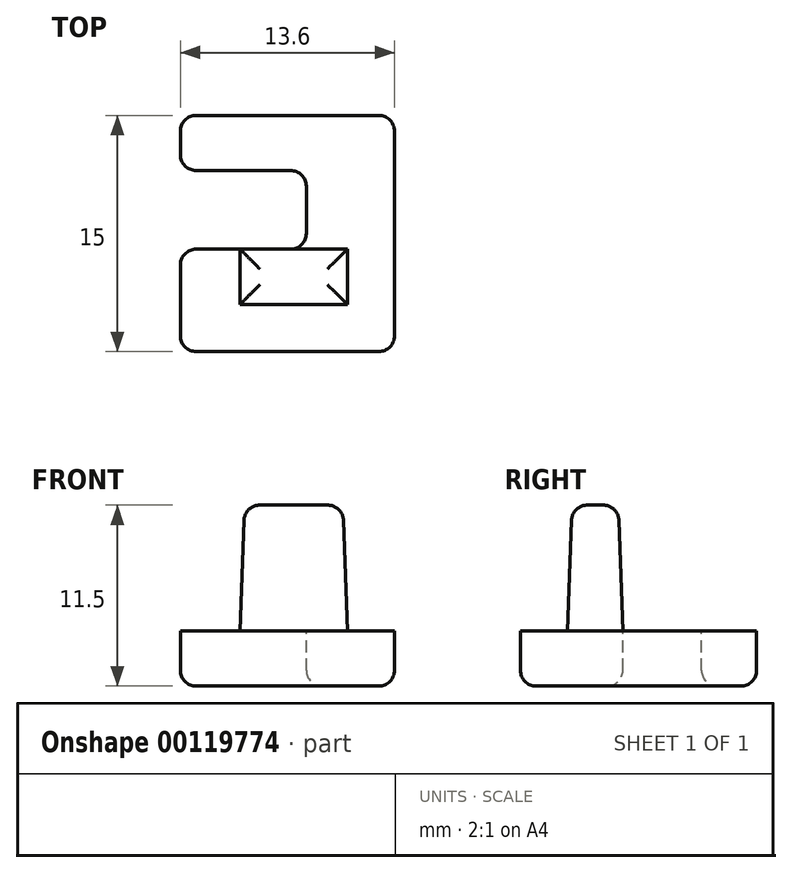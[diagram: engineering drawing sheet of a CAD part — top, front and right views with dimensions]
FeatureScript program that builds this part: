
annotation { "Feature Type Name" : "Feature", "Feature Type Description" : "" }
export const myFeature = defineFeature(function(context is Context, id is Id, definition is map)
    precondition{}
    {
        {
            var Q0;
            Q0=qCreatedBy(makeId("Top.planeOp"),FACE);
            var sketch = newSketch(context, id + "F0", { "sketchPlane" : qUnion([Q0])});
            skLineSegment(sketch, "E0.bottom", {"start": v(3.4, -1.75) * mm, "end": v(-3.4, -1.75) * mm});
            skLineSegment(sketch, "E0.top", {"start": v(3.4, 1.75) * mm, "end": v(-3.4, 1.75) * mm});
            skLineSegment(sketch, "E0.left", {"start": v(3.4, -1.75) * mm, "end": v(3.4, 1.75) * mm});
            skLineSegment(sketch, "E0.right", {"start": v(-3.4, -1.75) * mm, "end": v(-3.4, 1.75) * mm});
            skPoint(sketch, "E0.middle", {"position": v(0, 0) * mm});
            skSolve(sketch);
        }
        {
            var Q0;
            Q0 = qSketchRegion(id + "F0", true);
            extrude(context, id + "F1", {"entities" : qUnion([Q0]), "depth" : 8 * mm, "hasDraft" : true, "draftAngle" : 2 * degree, "draftPullDirection" : true});
        }
        {
            var Q0;
            Q0=makeQuery(id+"F1.opExtrude","CAP_FACE",FACE,{"disambiguationData":[OSD([sQuery(id+"F0.wireOp",EDGE,"E0.bottom"),sQuery(id+"F0.wireOp",EDGE,"E0.top"),sQuery(id+"F0.wireOp",EDGE,"E0.left"),sQuery(id+"F0.wireOp",EDGE,"E0.right")])],"isStart":true});
            var sketch = newSketch(context, id + "F2", { "sketchPlane" : qUnion([Q0])});
            skLineSegment(sketch, "E1.0", {"start": v(-0.2, -1.75) * mm, "end": v(-3.4, -1.75) * mm});
            skLineSegment(sketch, "E1.1", {"start": v(3.4, 1.75) * mm, "end": v(-3.4, 1.75) * mm, "construction": true});
            skLineSegment(sketch, "E1.2", {"start": v(3.4, 1.75) * mm, "end": v(3.4, -1.75) * mm, "construction": true});
            skLineSegment(sketch, "E1.3", {"start": v(-3.4, 1.75) * mm, "end": v(-3.4, -1.75) * mm, "construction": true});
            skLineSegment(sketch, "E2", {"start": v(-3.4, 4.75) * mm, "end": v(5.4, 4.75) * mm});
            skLineSegment(sketch, "E3", {"start": v(6.4, 3.75) * mm, "end": v(6.4, -4.75) * mm});
            skLineSegment(sketch, "E4", {"start": v(-3.4, -6.75) * mm, "end": v(-0.2, -6.75) * mm});
            skLineSegment(sketch, "E5", {"start": v(-3.67, -10.25) * mm, "end": v(5.4, -10.25) * mm});
            skLineSegment(sketch, "E6", {"start": v(6.4, -9.25) * mm, "end": v(6.4, -4.75) * mm});
            skLineSegment(sketch, "E7", {"start": v(-3.4, 4.75) * mm, "end": v(-6.2, 4.75) * mm});
            skLineSegment(sketch, "E8", {"start": v(-7.2, 3.75) * mm, "end": v(-7.2, -0.75) * mm});
            skLineSegment(sketch, "E9", {"start": v(-6.2, -1.75) * mm, "end": v(-3.4, -1.75) * mm});
            skLineSegment(sketch, "E10", {"start": v(-3.4, -6.75) * mm, "end": v(-6.2, -6.75) * mm});
            skLineSegment(sketch, "E11", {"start": v(-3.4, -10.25) * mm, "end": v(-6.2, -10.25) * mm});
            skLineSegment(sketch, "E12", {"start": v(-7.2, -9.25) * mm, "end": v(-7.2, -7.75) * mm});
            skLineSegment(sketch, "E13", {"start": v(0.8, -5.75) * mm, "end": v(0.8, -2.75) * mm});
            skPoint(sketch, "E14.visualSharp", {"position": v(-7.2, -10.25) * mm});
            skArc(sketch, "E14.filletArc", {"start": v(-7.2, -9.25) * mm, "mid": v(-6.9, -9.96) * mm, "end": v(-6.2, -10.25) * mm});
            skPoint(sketch, "E15.visualSharp", {"position": v(-7.2, -6.75) * mm});
            skArc(sketch, "E15.filletArc", {"start": v(-6.2, -6.75) * mm, "mid": v(-6.9, -7.04) * mm, "end": v(-7.2, -7.75) * mm});
            skPoint(sketch, "E16.visualSharp", {"position": v(6.4, -10.25) * mm});
            skArc(sketch, "E16.filletArc", {"start": v(5.4, -10.25) * mm, "mid": v(6.1, -9.96) * mm, "end": v(6.4, -9.25) * mm});
            skPoint(sketch, "E17.visualSharp", {"position": v(6.4, 4.75) * mm});
            skArc(sketch, "E17.filletArc", {"start": v(6.4, 3.75) * mm, "mid": v(6.1, 4.46) * mm, "end": v(5.4, 4.75) * mm});
            skPoint(sketch, "E18.visualSharp", {"position": v(-7.2, 4.75) * mm});
            skArc(sketch, "E18.filletArc", {"start": v(-6.2, 4.75) * mm, "mid": v(-6.9, 4.46) * mm, "end": v(-7.2, 3.75) * mm});
            skPoint(sketch, "E19.visualSharp", {"position": v(-7.2, -1.75) * mm});
            skArc(sketch, "E19.filletArc", {"start": v(-7.2, -0.75) * mm, "mid": v(-6.9, -1.46) * mm, "end": v(-6.2, -1.75) * mm});
            skPoint(sketch, "E20.visualSharp", {"position": v(0.8, -6.75) * mm});
            skArc(sketch, "E20.filletArc", {"start": v(-0.2, -6.75) * mm, "mid": v(0.5, -6.46) * mm, "end": v(0.8, -5.75) * mm});
            skPoint(sketch, "E21.newPointA", {"position": v(0.8, -1.75) * mm});
            skPoint(sketch, "E21.newPointB", {"position": v(3.4, -1.75) * mm});
            skArc(sketch, "E21.filletArc", {"start": v(0.8, -2.75) * mm, "mid": v(0.5, -2.04) * mm, "end": v(-0.2, -1.75) * mm});
            skSolve(sketch);
        }
        {
            var Q0;
            Q0=makeQuery(id+"F2.imprint","IMPRINT",FACE,{"disambiguationData":[TD([[makeQuery(id+"F2.imprint","IMPRINT",EDGE,{"derivedFrom":sQuery(id+"F2.wireOp",EDGE,"E2")}),-1.0]])]});
            var Q1;
            {var subQ2=sQuery(id+"F2.wireOp",EDGE,"E1.0");Q1=makeQuery(id+"F2.imprint","IMPRINT",FACE,{"disambiguationData":[TD([[makeQuery(id+"F2.imprint","IMPRINT",EDGE,{"derivedFrom":subQ2}),-1.0]])]});}
            extrude(context, id + "F3", {"entities" : qUnion([Q0, Q1]), "operationType" : NewBodyOperationType.ADD, "depth" : 3.5 * mm});
        }
        {
            var Q0;
            Q0=makeQuery(id+"F3.opExtrude","CAP_EDGE",EDGE,{"disambiguationData":[OSD([sQuery(id+"F2.wireOp",EDGE,"E5"),sQuery(id+"F2.wireOp",EDGE,"E11")])],"isStart":false});
            var Q1;
            Q1=makeQuery(id+"F1.opExtrude","CAP_EDGE",EDGE,{"disambiguationData":[OSD([sQuery(id+"F0.wireOp",EDGE,"E0.top")])],"isStart":false});
            var Q2;
            Q2=makeQuery(id+"F1.opExtrude","CAP_EDGE",EDGE,{"disambiguationData":[OSD([sQuery(id+"F0.wireOp",EDGE,"E0.bottom")])],"isStart":false});
            var Q3;
            Q3=makeQuery(id+"F1.opExtrude","CAP_EDGE",EDGE,{"disambiguationData":[OSD([sQuery(id+"F0.wireOp",EDGE,"E0.right")])],"isStart":false});
            var Q4;
            Q4=makeQuery(id+"F1.opExtrude","CAP_EDGE",EDGE,{"disambiguationData":[OSD([sQuery(id+"F0.wireOp",EDGE,"E0.left")])],"isStart":false});
            fillet(context, id + "F4", {"entities" : qUnion([Q0, Q1, Q2, Q3, Q4]), "radius" : 1 * mm, "tangentPropagation" : true, "allowEdgeOverflow" : false});
        }
    });
